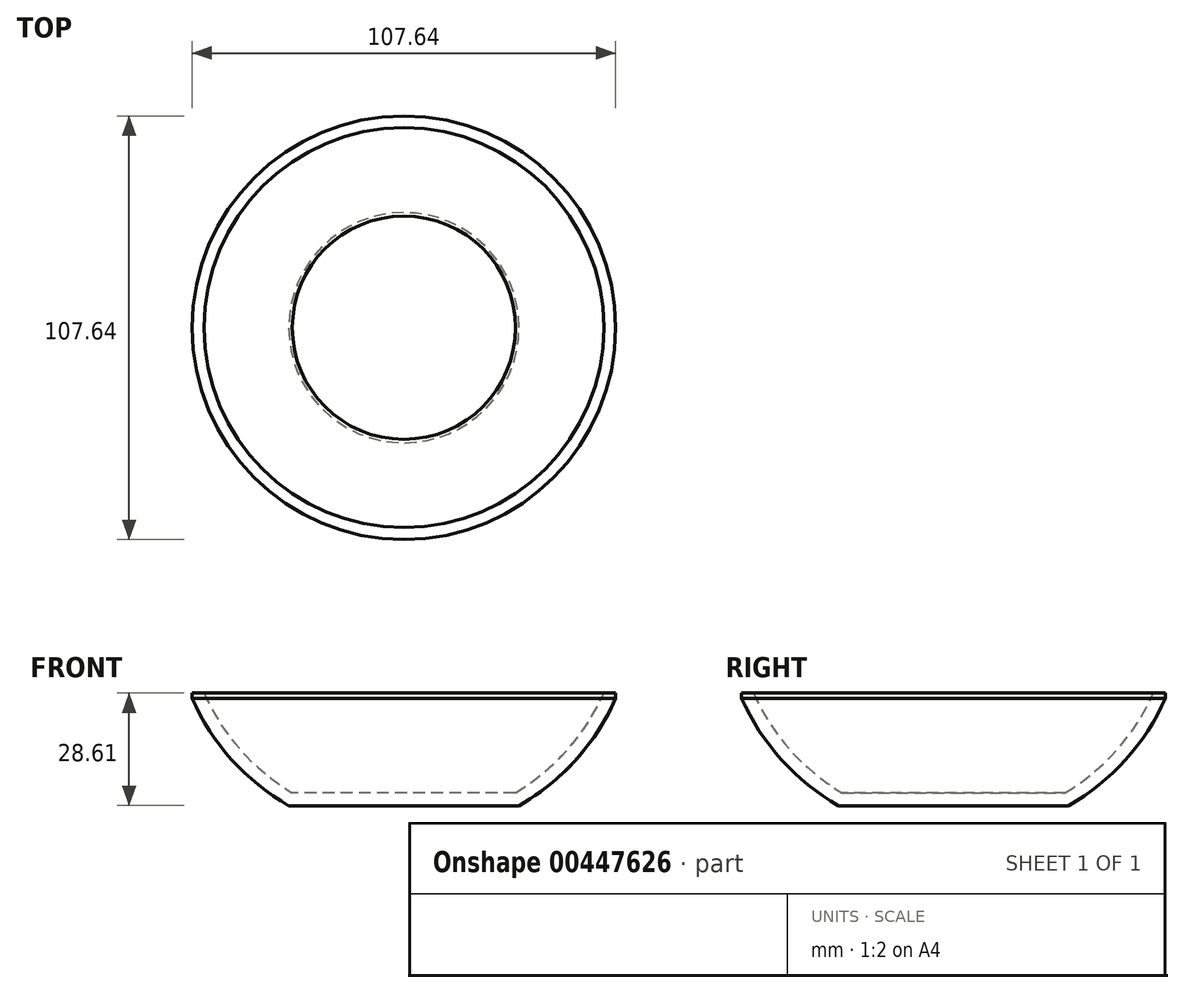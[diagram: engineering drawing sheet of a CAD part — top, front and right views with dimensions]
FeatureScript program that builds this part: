
annotation { "Feature Type Name" : "Feature", "Feature Type Description" : "" }
export const myFeature = defineFeature(function(context is Context, id is Id, definition is map)
    precondition{}
    {
        {
            var Q0;
            Q0=qCreatedBy(makeId("Front.planeOp"),FACE);
            var sketch = newSketch(context, id + "F0", { "sketchPlane" : qUnion([Q0])});
            skArc(sketch, "E0", {"start": v(-101.6, 0) * mm, "mid": v(-92.35, -14.4) * mm, "end": v(-79.16, -25.31) * mm});
            skLineSegment(sketch, "E1", {"start": v(-79.16, -25.31) * mm, "end": v(-50.8, -25.31) * mm});
            skLineSegment(sketch, "E2.1", {"start": v(-80.05, -28.61) * mm, "end": v(-50.8, -28.61) * mm});
            skArc(sketch, "E2.2", {"start": v(-104.62, -1.33) * mm, "mid": v(-94.52, -16.94) * mm, "end": v(-80.05, -28.61) * mm});
            skLineSegment(sketch, "E3", {"start": v(-101.6, 0) * mm, "end": v(-104.62, 0) * mm});
            skLineSegment(sketch, "E4", {"start": v(-104.62, 0) * mm, "end": v(-104.62, -1.33) * mm});
            skLineSegment(sketch, "E5", {"start": v(-50.8, -25.31) * mm, "end": v(-50.8, -28.61) * mm});
            skPoint(sketch, "E6.trimOffspring.start.orphan", {"position": v(-22.44, -25.31) * mm});
            skPoint(sketch, "E2.0.start.orphan", {"position": v(-21.55, -28.61) * mm});
            skPoint(sketch, "E7.start.orphan", {"position": v(0, 0) * mm});
            skPoint(sketch, "E8.end.orphan", {"position": v(3.02, -1.33) * mm});
            skPoint(sketch, "E8.start.orphan", {"position": v(3.02, 0) * mm});
            skSolve(sketch);
        }
        {
            var Q0;
            Q0=makeQuery(id+"F0.imprint","IMPRINT",FACE,{"disambiguationData":[TD([[makeQuery(id+"F0.imprint","IMPRINT",EDGE,{"derivedFrom":sQuery(id+"F0.wireOp",EDGE,"E0")}),-1.0]])]});
            var Q1;
            Q1=sQuery(id+"F0.wireOp",EDGE,"E5");
            revolve(context, id + "F1", {"entities" : qUnion([Q0]), "axis" : qUnion([Q1]), "revolveType" : RevolveType.FULL});
        }
    });
